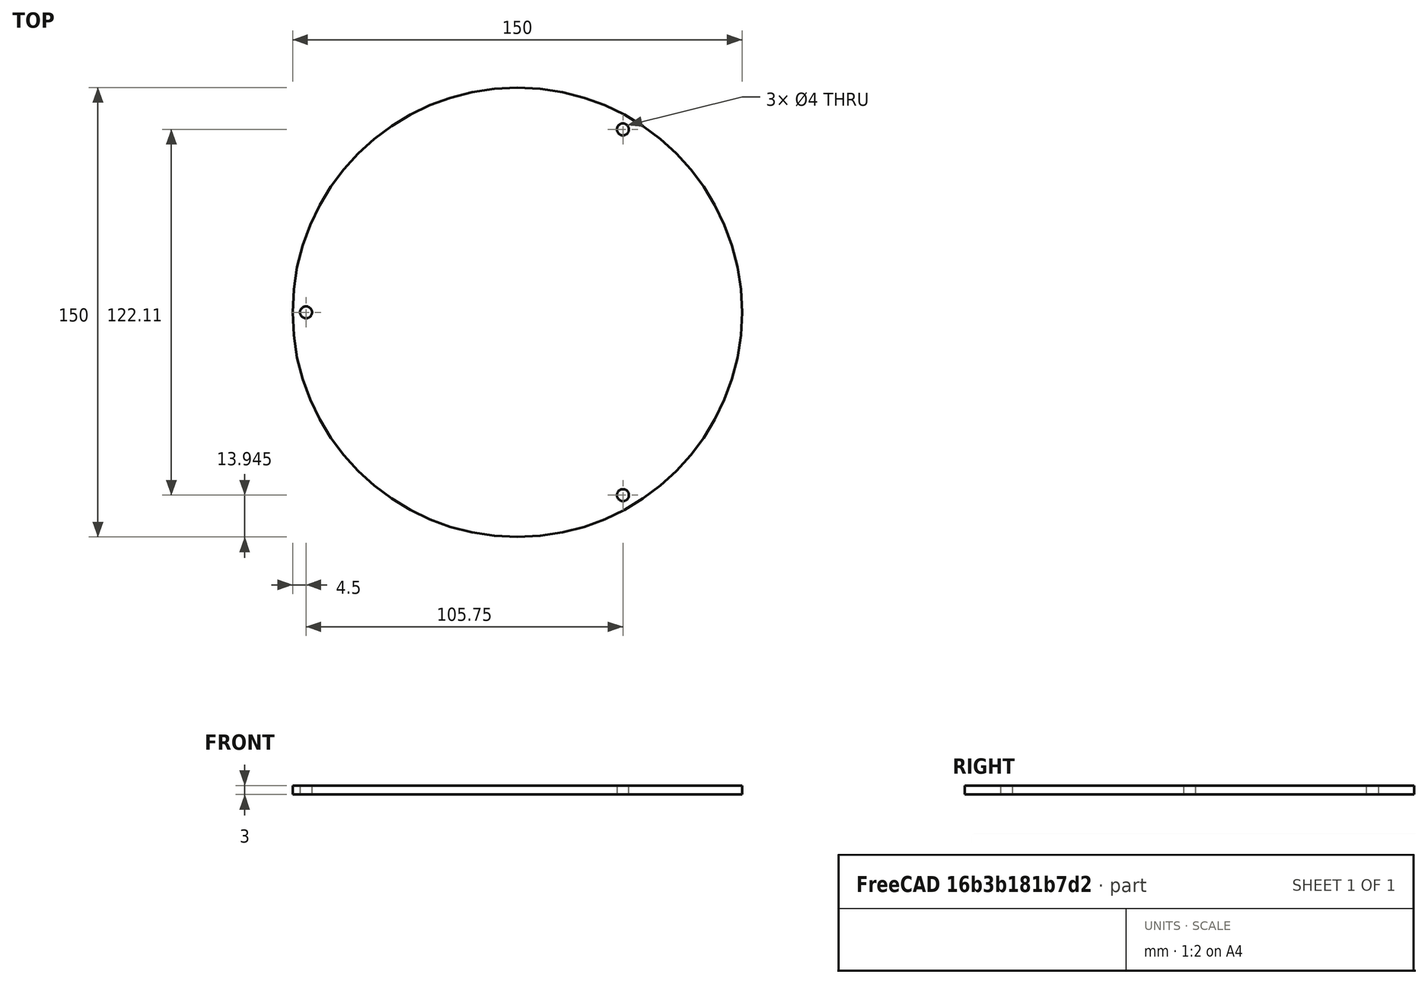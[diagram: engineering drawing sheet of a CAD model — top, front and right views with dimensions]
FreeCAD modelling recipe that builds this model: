
FCSTD DOCUMENT  (FreeCAD 0.20R29410 (Git))
Label: cover_disc_150mm
License: All rights reserved
LicenseURL: http://en.wikipedia.org/wiki/All_rights_reserved
objects: Sketcher::SketchObject×1, PartDesign::Pad×1, PartDesign::Body×1
note: 4 computed .brp shape members not serialized (recipe doc carries the construction recipe); baked Part::Feature solids carry a one-line shape summary decoded from their .brp

FEATURE [Sketcher::SketchObject] Sketch
  FullyConstrained = true
  MapMode = 5
  Support = -> [XY_Plane]
  sketch-geometry (9):
    g0: Circle CenterX=0 CenterY=0 CenterZ=0 NormalX=0 NormalY=0 NormalZ=1 AngleXU=0 Radius=75
    g1: Circle CenterX=-70.5 CenterY=0 CenterZ=0 NormalX=0 NormalY=0 NormalZ=1 AngleXU=0 Radius=2
    g2: Circle CenterX=0 CenterY=0 CenterZ=0 NormalX=0 NormalY=0 NormalZ=1 AngleXU=0 Radius=70.5
    g3: LineSegment StartX=-75 StartY=0 StartZ=0 EndX=-72.5 EndY=0 EndZ=0
    g4: Circle CenterX=35.25 CenterY=61.0548 CenterZ=0 NormalX=0 NormalY=0 NormalZ=1 AngleXU=0 Radius=2
    g5: Circle CenterX=35.25 CenterY=-61.0548 CenterZ=0 NormalX=0 NormalY=0 NormalZ=1 AngleXU=0 Radius=2
    g6: LineSegment StartX=35.25 StartY=61.0548 StartZ=0 EndX=35.25 EndY=-61.0548 EndZ=0
    g7: LineSegment StartX=35.25 StartY=-61.0548 StartZ=0 EndX=-70.5 EndY=0 EndZ=0
    g8: LineSegment StartX=-70.5 StartY=0 StartZ=0 EndX=35.25 EndY=61.0548 EndZ=0
  constraints (23):
    c: Coincident(g0,g-1)
    c: PointOnObject(g1,g-1)
    c: Coincident(g2,g0)
    c: Diameter(g0) = 150  'diameter'
    c: Horizontal(g3)
    c: PointOnObject(g3,g0)
    c: PointOnObject(g3,g-1)
    c: DistanceX(g3,g3) = 2.5
    c: Equal(g1,g4)
    c: Equal(g4,g5)
    c: Diameter(g5) = 4
    c: PointOnObject(g4,g2)
    c: PointOnObject(g5,g2)
    c: Coincident(g6,g4)
    c: Coincident(g6,g5)
    c: Coincident(g7,g5)
    c: Coincident(g8,g4)
    c: Equal(g8,g6)
    c: Equal(g6,g7)
    c: PointOnObject(g1,g2)
    c: Coincident(g8,g1)
    c: Coincident(g7,g1)
    c: PointOnObject(g3,g1)
FEATURE [PartDesign::Pad] Pad
  Direction = (0,0,1)
  Length = 3
  Length2 = 10
  Profile = -> Sketch
  ReferenceAxis = -> Sketch [N_Axis]
  Type = 0
FEATURE [PartDesign::Body] Body
  Group = -> [Sketch,Pad]
  Origin = -> Origin
  Tip = -> Pad
